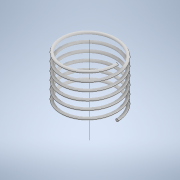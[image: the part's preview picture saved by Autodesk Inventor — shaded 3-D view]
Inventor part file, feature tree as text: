
AUTODESK INVENTOR PART (.ipt)
format: ipt  version: 2020 (Build 240168000, 168)  size: 265,728 bytes
history: native  units: mm
features: helix x1, other x1, sketch x1
ambient origin geometry x8: Origin, YZ Plane, XZ Plane, XY Plane, X Axis, Y Axis, Z Axis, Center Point
bodies: Solid1 (feature_tree)
feature tree (3):
  helix  "Coil1"  [1 undecoded]
  other  "Work Axis1"
  sketch  "Sketch1"  dims[d1=1.0mm d2=3.0mm d3=18.0mm d4=10.0mm d5=0.0mm d6=90.0deg d7=90.0deg d8=0.0mm d9=0.0mm]
note: 1 required parameter value undecoded (feature->parameter linkage not recoverable at this tier; creation-order binding heuristic only, values carry confidence <= 0.55)
